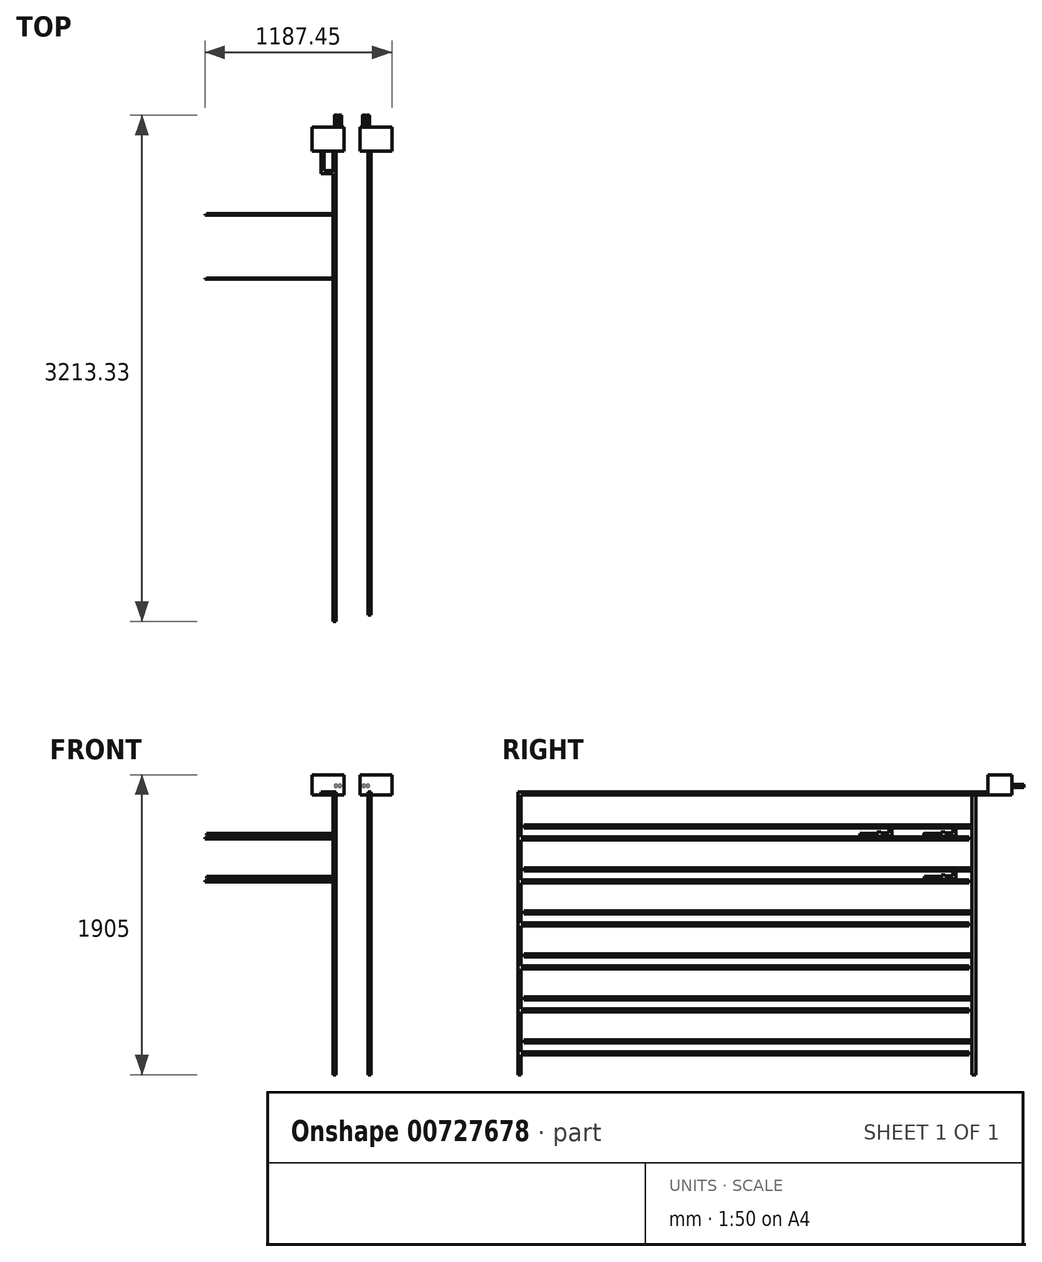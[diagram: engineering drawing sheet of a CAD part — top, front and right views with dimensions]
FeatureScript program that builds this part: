
annotation { "Feature Type Name" : "Feature", "Feature Type Description" : "" }
export const myFeature = defineFeature(function(context is Context, id is Id, definition is map)
    precondition{}
    {
        {
            var Q0;
            Q0=qCreatedBy(makeId("Top.planeOp"),FACE);
            var sketch = newSketch(context, id + "F0", { "sketchPlane" : qUnion([Q0])});
            skLineSegment(sketch, "E0.bottom", {"start": v(0, 0) * mm, "end": v(-1117.6, 0) * mm});
            skLineSegment(sketch, "E0.top", {"start": v(0, 2844.8) * mm, "end": v(-1117.6, 2844.8) * mm});
            skLineSegment(sketch, "E0.right", {"start": v(-1117.6, 0) * mm, "end": v(-1117.6, 2844.8) * mm});
            skLineSegment(sketch, "E1.bottom", {"start": v(0, 0) * mm, "end": v(1117.6, 0) * mm});
            skLineSegment(sketch, "E1.top", {"start": v(0, 2844.8) * mm, "end": v(1117.6, 2844.8) * mm});
            skLineSegment(sketch, "E1.right", {"start": v(1117.6, 0) * mm, "end": v(1117.6, 2844.8) * mm});
            skLineSegment(sketch, "E2.bottom", {"start": v(-101.6, 2844.8) * mm, "end": v(101.6, 2844.8) * mm});
            skLineSegment(sketch, "E2.top", {"start": v(-101.6, 0) * mm, "end": v(101.6, 0) * mm});
            skLineSegment(sketch, "E2.left", {"start": v(-101.6, 2641.6) * mm, "end": v(-101.6, 203.2) * mm});
            skLineSegment(sketch, "E2.right", {"start": v(101.6, 2641.6) * mm, "end": v(101.6, 203.2) * mm});
            skLineSegment(sketch, "E3", {"start": v(-1117.6, 2641.6) * mm, "end": v(-101.6, 2641.6) * mm});
            skLineSegment(sketch, "E4", {"start": v(-1117.6, 2235.2) * mm, "end": v(-101.6, 2235.2) * mm});
            skLineSegment(sketch, "E5", {"start": v(-1117.6, 1828.8) * mm, "end": v(-101.6, 1828.8) * mm});
            skLineSegment(sketch, "E6", {"start": v(-1117.6, 1422.4) * mm, "end": v(-101.6, 1422.4) * mm});
            skLineSegment(sketch, "E7", {"start": v(-1117.6, 1016) * mm, "end": v(-101.6, 1016) * mm});
            skLineSegment(sketch, "E8", {"start": v(-1117.6, 609.6) * mm, "end": v(-101.6, 609.6) * mm});
            skLineSegment(sketch, "E9", {"start": v(-1117.6, 203.2) * mm, "end": v(-101.6, 203.2) * mm});
            skLineSegment(sketch, "E10.trimOffspring", {"start": v(101.6, 2641.6) * mm, "end": v(1117.6, 2641.6) * mm});
            skLineSegment(sketch, "E11.trimOffspring", {"start": v(101.6, 2235.2) * mm, "end": v(1117.6, 2235.2) * mm});
            skLineSegment(sketch, "E12.trimOffspring", {"start": v(101.6, 1828.8) * mm, "end": v(1117.6, 1828.8) * mm});
            skLineSegment(sketch, "E13.trimOffspring", {"start": v(101.6, 1422.4) * mm, "end": v(1117.6, 1422.4) * mm});
            skLineSegment(sketch, "E14.trimOffspring", {"start": v(101.6, 1016) * mm, "end": v(1117.6, 1016) * mm});
            skLineSegment(sketch, "E15.trimOffspring", {"start": v(101.6, 609.6) * mm, "end": v(1117.6, 609.6) * mm});
            skLineSegment(sketch, "E16.trimOffspring", {"start": v(101.6, 203.2) * mm, "end": v(1117.6, 203.2) * mm});
            skLineSegment(sketch, "E17", {"start": v(-101.6, 2641.6) * mm, "end": v(101.6, 2641.6) * mm});
            skLineSegment(sketch, "E18.bottom", {"start": v(3130.62, 2641.6) * mm, "end": v(3333.82, 2641.6) * mm});
            skLineSegment(sketch, "E18.top", {"start": v(3130.62, 2794) * mm, "end": v(3333.82, 2794) * mm});
            skLineSegment(sketch, "E18.left", {"start": v(3130.62, 2641.6) * mm, "end": v(3130.62, 2794) * mm});
            skLineSegment(sketch, "E18.right", {"start": v(3333.82, 2641.6) * mm, "end": v(3333.82, 2794) * mm});
            skLineSegment(sketch, "E19.bottom", {"start": v(3435.42, 2641.6) * mm, "end": v(3638.62, 2641.6) * mm});
            skLineSegment(sketch, "E19.top", {"start": v(3435.42, 2794) * mm, "end": v(3638.62, 2794) * mm});
            skLineSegment(sketch, "E19.left", {"start": v(3435.42, 2641.6) * mm, "end": v(3435.42, 2794) * mm});
            skLineSegment(sketch, "E19.right", {"start": v(3638.62, 2641.6) * mm, "end": v(3638.62, 2794) * mm});
            skLineSegment(sketch, "E20", {"start": v(-812.8, 2641.6) * mm, "end": v(-812.8, 203.2) * mm});
            skLineSegment(sketch, "E21", {"start": v(-609.6, 2641.6) * mm, "end": v(-609.6, 203.2) * mm});
            skSolve(sketch);
        }
        {
            var Q0;
            Q0=makeQuery(id+"F0.imprint","IMPRINT",FACE,{"disambiguationData":[TD([[makeQuery(id+"F0.imprint","IMPRINT",EDGE,{"derivedFrom":sQuery(id+"F0.wireOp",EDGE,"E18.bottom")}),1.0]])]});
            extrude(context, id + "F1", {"entities" : qUnion([Q0]), "depth" : 127 * mm, "offsetDistance" : 25.4 * mm});
        }
        {
            var Q0;
            Q0=makeQuery(id+"F0.imprint","IMPRINT",FACE,{"disambiguationData":[TD([[makeQuery(id+"F0.imprint","IMPRINT",EDGE,{"derivedFrom":sQuery(id+"F0.wireOp",EDGE,"E19.bottom")}),1.0]])]});
            extrude(context, id + "F2", {"entities" : qUnion([Q0]), "depth" : 127 * mm, "offsetDistance" : 25.4 * mm});
        }
        {
            var Q0;
            Q0=makeQuery(id+"F1.opExtrude","SWEPT_FACE",FACE,{"disambiguationData":[OSD([sQuery(id+"F0.wireOp",EDGE,"E18.bottom")])]});
            var sketch = newSketch(context, id + "F3", { "sketchPlane" : qUnion([Q0])});
            skLineSegment(sketch, "E22.bottom", {"start": v(3283.02, 0) * mm, "end": v(3263.97, 0) * mm});
            skLineSegment(sketch, "E22.top", {"start": v(3283.02, 19.05) * mm, "end": v(3263.97, 19.05) * mm});
            skLineSegment(sketch, "E22.left", {"start": v(3283.02, 0) * mm, "end": v(3283.02, 19.05) * mm});
            skLineSegment(sketch, "E22.right", {"start": v(3263.97, 0) * mm, "end": v(3263.97, 19.05) * mm});
            skPoint(sketch, "E23.top.end.orphan", {"position": v(3416.06, 19.05) * mm});
            skPoint(sketch, "E23.left.start.orphan", {"position": v(3397.68, 0) * mm});
            skLineSegment(sketch, "E24.bottom", {"start": v(3486.22, 0) * mm, "end": v(3505.27, 0) * mm});
            skLineSegment(sketch, "E24.top", {"start": v(3486.22, 19.05) * mm, "end": v(3505.27, 19.05) * mm});
            skLineSegment(sketch, "E24.left", {"start": v(3486.22, 0) * mm, "end": v(3486.22, 19.05) * mm});
            skLineSegment(sketch, "E24.right", {"start": v(3505.27, 0) * mm, "end": v(3505.27, 19.05) * mm});
            skSolve(sketch);
        }
        {
            var Q0;
            Q0 = qSketchRegion(id + "F3", true);
            extrude(context, id + "F4", {"entities" : qUnion([Q0]), "depth" : 101.6 * mm, "offsetDistance" : 25.4 * mm});
        }
        {
            var Q0;
            Q0=makeQuery(id+"F4.opExtrude","SWEPT_FACE",FACE,{"disambiguationData":[OSD([sQuery(id+"F3.wireOp",EDGE,"E22.bottom")])]});
            var sketch = newSketch(context, id + "F5", { "sketchPlane" : qUnion([Q0])});
            skLineSegment(sketch, "E25.bottom", {"start": v(3263.97, -2540) * mm, "end": v(3283.02, -2540) * mm});
            skLineSegment(sketch, "E25.top", {"start": v(3263.97, -2565.4) * mm, "end": v(3283.02, -2565.4) * mm});
            skLineSegment(sketch, "E25.left", {"start": v(3263.97, -2540) * mm, "end": v(3263.97, -2565.4) * mm});
            skLineSegment(sketch, "E25.right", {"start": v(3283.02, -2540) * mm, "end": v(3283.02, -2565.4) * mm});
            skLineSegment(sketch, "E26.bottom", {"start": v(3486.22, -2540) * mm, "end": v(3505.27, -2540) * mm});
            skLineSegment(sketch, "E26.top", {"start": v(3486.22, -2565.4) * mm, "end": v(3505.27, -2565.4) * mm});
            skLineSegment(sketch, "E26.left", {"start": v(3486.22, -2540) * mm, "end": v(3486.22, -2565.4) * mm});
            skLineSegment(sketch, "E26.right", {"start": v(3505.27, -2540) * mm, "end": v(3505.27, -2565.4) * mm});
            skSolve(sketch);
        }
        {
            var Q0;
            Q0 = qSketchRegion(id + "F5", true);
            extrude(context, id + "F6", {"entities" : qUnion([Q0]), "depth" : 1778 * mm, "offsetDistance" : 25.4 * mm});
        }
        {
            var Q0;
            Q0=makeQuery(id+"F6.opExtrude","SWEPT_FACE",FACE,{"disambiguationData":[OSD([sQuery(id+"F5.wireOp",EDGE,"E25.bottom")])]});
            var sketch = newSketch(context, id + "F7", { "sketchPlane" : qUnion([Q0])});
            skLineSegment(sketch, "E27.bottom", {"start": v(3263.97, -190.5) * mm, "end": v(3283.02, -190.5) * mm});
            skLineSegment(sketch, "E27.top", {"start": v(3263.97, -209.55) * mm, "end": v(3283.02, -209.55) * mm});
            skLineSegment(sketch, "E27.left", {"start": v(3263.97, -190.5) * mm, "end": v(3263.97, -209.55) * mm});
            skLineSegment(sketch, "E27.right", {"start": v(3283.02, -190.5) * mm, "end": v(3283.02, -209.55) * mm});
            skLineSegment(sketch, "E28.bottom", {"start": v(3263.97, -463.55) * mm, "end": v(3283.02, -463.55) * mm});
            skLineSegment(sketch, "E28.top", {"start": v(3263.97, -482.6) * mm, "end": v(3283.02, -482.6) * mm});
            skLineSegment(sketch, "E28.left", {"start": v(3263.97, -463.55) * mm, "end": v(3263.97, -482.6) * mm});
            skLineSegment(sketch, "E28.right", {"start": v(3283.02, -463.55) * mm, "end": v(3283.02, -482.6) * mm});
            skLineSegment(sketch, "E29.bottom", {"start": v(3263.97, -736.6) * mm, "end": v(3283.02, -736.6) * mm});
            skLineSegment(sketch, "E29.top", {"start": v(3263.97, -755.65) * mm, "end": v(3283.02, -755.65) * mm});
            skLineSegment(sketch, "E29.left", {"start": v(3263.97, -736.6) * mm, "end": v(3263.97, -755.65) * mm});
            skLineSegment(sketch, "E29.right", {"start": v(3283.02, -736.6) * mm, "end": v(3283.02, -755.65) * mm});
            skLineSegment(sketch, "E30.bottom", {"start": v(3263.97, -1009.65) * mm, "end": v(3283.02, -1009.65) * mm});
            skLineSegment(sketch, "E30.top", {"start": v(3263.97, -1028.7) * mm, "end": v(3283.02, -1028.7) * mm});
            skLineSegment(sketch, "E30.left", {"start": v(3263.97, -1009.65) * mm, "end": v(3263.97, -1028.7) * mm});
            skLineSegment(sketch, "E30.right", {"start": v(3283.02, -1009.65) * mm, "end": v(3283.02, -1028.7) * mm});
            skLineSegment(sketch, "E31.bottom", {"start": v(3263.97, -1282.7) * mm, "end": v(3283.02, -1282.7) * mm});
            skLineSegment(sketch, "E31.top", {"start": v(3263.97, -1301.75) * mm, "end": v(3283.02, -1301.75) * mm});
            skLineSegment(sketch, "E31.left", {"start": v(3263.97, -1282.7) * mm, "end": v(3263.97, -1301.75) * mm});
            skLineSegment(sketch, "E31.right", {"start": v(3283.02, -1282.7) * mm, "end": v(3283.02, -1301.75) * mm});
            skLineSegment(sketch, "E32.bottom", {"start": v(3263.97, -1555.75) * mm, "end": v(3283.02, -1555.75) * mm});
            skLineSegment(sketch, "E32.top", {"start": v(3263.97, -1574.8) * mm, "end": v(3283.02, -1574.8) * mm});
            skLineSegment(sketch, "E32.left", {"start": v(3263.97, -1555.75) * mm, "end": v(3263.97, -1574.8) * mm});
            skLineSegment(sketch, "E32.right", {"start": v(3283.02, -1555.75) * mm, "end": v(3283.02, -1574.8) * mm});
            skLineSegment(sketch, "E33.bottom", {"start": v(3486.22, -190.5) * mm, "end": v(3505.27, -190.5) * mm});
            skLineSegment(sketch, "E33.top", {"start": v(3486.22, -209.55) * mm, "end": v(3505.27, -209.55) * mm});
            skLineSegment(sketch, "E33.left", {"start": v(3486.22, -190.5) * mm, "end": v(3486.22, -209.55) * mm});
            skLineSegment(sketch, "E33.right", {"start": v(3505.27, -190.5) * mm, "end": v(3505.27, -209.55) * mm});
            skLineSegment(sketch, "E34.bottom", {"start": v(3486.22, -463.55) * mm, "end": v(3505.27, -463.55) * mm});
            skLineSegment(sketch, "E34.top", {"start": v(3486.22, -482.6) * mm, "end": v(3505.27, -482.6) * mm});
            skLineSegment(sketch, "E34.left", {"start": v(3486.22, -463.55) * mm, "end": v(3486.22, -482.6) * mm});
            skLineSegment(sketch, "E34.right", {"start": v(3505.27, -463.55) * mm, "end": v(3505.27, -482.6) * mm});
            skLineSegment(sketch, "E35.bottom", {"start": v(3486.22, -736.6) * mm, "end": v(3505.27, -736.6) * mm});
            skLineSegment(sketch, "E35.top", {"start": v(3486.22, -755.65) * mm, "end": v(3505.27, -755.65) * mm});
            skLineSegment(sketch, "E35.left", {"start": v(3486.22, -736.6) * mm, "end": v(3486.22, -755.65) * mm});
            skLineSegment(sketch, "E35.right", {"start": v(3505.27, -736.6) * mm, "end": v(3505.27, -755.65) * mm});
            skLineSegment(sketch, "E36.bottom", {"start": v(3486.22, -1009.65) * mm, "end": v(3505.27, -1009.65) * mm});
            skLineSegment(sketch, "E36.top", {"start": v(3486.22, -1028.7) * mm, "end": v(3505.27, -1028.7) * mm});
            skLineSegment(sketch, "E36.left", {"start": v(3486.22, -1009.65) * mm, "end": v(3486.22, -1028.7) * mm});
            skLineSegment(sketch, "E36.right", {"start": v(3505.27, -1009.65) * mm, "end": v(3505.27, -1028.7) * mm});
            skLineSegment(sketch, "E37.bottom", {"start": v(3486.22, -1282.7) * mm, "end": v(3505.27, -1282.7) * mm});
            skLineSegment(sketch, "E37.top", {"start": v(3486.22, -1301.75) * mm, "end": v(3505.27, -1301.75) * mm});
            skLineSegment(sketch, "E37.left", {"start": v(3486.22, -1282.7) * mm, "end": v(3486.22, -1301.75) * mm});
            skLineSegment(sketch, "E37.right", {"start": v(3505.27, -1282.7) * mm, "end": v(3505.27, -1301.75) * mm});
            skLineSegment(sketch, "E38.bottom", {"start": v(3486.22, -1555.75) * mm, "end": v(3505.27, -1555.75) * mm});
            skLineSegment(sketch, "E38.top", {"start": v(3486.22, -1574.8) * mm, "end": v(3505.27, -1574.8) * mm});
            skLineSegment(sketch, "E38.left", {"start": v(3486.22, -1555.75) * mm, "end": v(3486.22, -1574.8) * mm});
            skLineSegment(sketch, "E38.right", {"start": v(3505.27, -1555.75) * mm, "end": v(3505.27, -1574.8) * mm});
            skSolve(sketch);
        }
        {
            var Q0;
            Q0 = qSketchRegion(id + "F7", true);
            extrude(context, id + "F8", {"entities" : qUnion([Q0]), "depth" : 2844.8 * mm, "offsetDistance" : 25.4 * mm});
        }
        {
            var Q0;
            Q0=makeQuery(id+"F8.opExtrude","SWEPT_FACE",FACE,{"disambiguationData":[OSD([sQuery(id+"F7.wireOp",EDGE,"E27.top")])]});
            var sketch = newSketch(context, id + "F9", { "sketchPlane" : qUnion([Q0])});
            skLineSegment(sketch, "E39.bottom", {"start": v(3263.97, -2438.4) * mm, "end": v(3283.02, -2438.4) * mm});
            skLineSegment(sketch, "E39.top", {"start": v(3263.97, -2419.35) * mm, "end": v(3283.02, -2419.35) * mm});
            skLineSegment(sketch, "E39.left", {"start": v(3263.97, -2438.4) * mm, "end": v(3263.97, -2419.35) * mm});
            skLineSegment(sketch, "E39.right", {"start": v(3283.02, -2438.4) * mm, "end": v(3283.02, -2419.35) * mm});
            skSolve(sketch);
        }
        {
            var Q0;
            Q0 = qSketchRegion(id + "F9", true);
            extrude(context, id + "F10", {"entities" : qUnion([Q0]), "operationType" : NewBodyOperationType.ADD, "depth" : 50.8 * mm, "offsetDistance" : 25.4 * mm});
        }
        {
            var Q0;
            Q0=makeQuery(id+"F10.opExtrude","SWEPT_FACE",FACE,{"disambiguationData":[OSD([sQuery(id+"F9.wireOp",EDGE,"E39.top")])]});
            var sketch = newSketch(context, id + "F11", { "sketchPlane" : qUnion([Q0])});
            skLineSegment(sketch, "E40.bottom", {"start": v(3263.97, -260.35) * mm, "end": v(3283.02, -260.35) * mm});
            skLineSegment(sketch, "E40.top", {"start": v(3263.97, -241.3) * mm, "end": v(3283.02, -241.3) * mm});
            skLineSegment(sketch, "E40.left", {"start": v(3263.97, -260.35) * mm, "end": v(3263.97, -241.3) * mm});
            skLineSegment(sketch, "E40.right", {"start": v(3283.02, -260.35) * mm, "end": v(3283.02, -241.3) * mm});
            skSolve(sketch);
        }
        {
            var Q0;
            Q0 = qSketchRegion(id + "F11", true);
            extrude(context, id + "F12", {"entities" : qUnion([Q0]), "operationType" : NewBodyOperationType.ADD, "depth" : 50.8 * mm, "offsetDistance" : 25.4 * mm});
        }
        {
            var Q0;
            Q0=makeQuery(id+"F12.opExtrude","CAP_FACE",FACE,{"disambiguationData":[OSD([sQuery(id+"F11.wireOp",EDGE,"E40.bottom"),sQuery(id+"F11.wireOp",EDGE,"E40.top"),sQuery(id+"F11.wireOp",EDGE,"E40.left"),sQuery(id+"F11.wireOp",EDGE,"E40.right")])],"isStart":false});
            var sketch = newSketch(context, id + "F13", { "sketchPlane" : qUnion([Q0])});
            skLineSegment(sketch, "E41.bottom", {"start": v(3263.97, -264.58) * mm, "end": v(3283.02, -264.58) * mm});
            skLineSegment(sketch, "E41.top", {"start": v(3263.97, -237.07) * mm, "end": v(3283.02, -237.07) * mm});
            skLineSegment(sketch, "E41.left", {"start": v(3263.97, -264.58) * mm, "end": v(3263.97, -237.07) * mm});
            skLineSegment(sketch, "E41.right", {"start": v(3283.02, -264.58) * mm, "end": v(3283.02, -237.07) * mm});
            skSolve(sketch);
        }
        {
            var Q0;
            Q0 = qSketchRegion(id + "F13", true);
            extrude(context, id + "F14", {"entities" : qUnion([Q0]), "operationType" : NewBodyOperationType.ADD, "depth" : 25.4 * mm, "offsetDistance" : 25.4 * mm});
        }
        {
            var Q0;
            Q0=makeQuery(id+"F14.opExtrude","CAP_FACE",FACE,{"disambiguationData":[OSD([sQuery(id+"F13.wireOp",EDGE,"E41.bottom"),sQuery(id+"F13.wireOp",EDGE,"E41.top"),sQuery(id+"F13.wireOp",EDGE,"E41.left"),sQuery(id+"F13.wireOp",EDGE,"E41.right")])],"isStart":false});
            var sketch = newSketch(context, id + "F15", { "sketchPlane" : qUnion([Q0])});
            skCircle(sketch, "E42", {"center": v(3273.5, -250.83) * mm, "radius": 4.23 * mm});
            skSolve(sketch);
        }
        {
            var Q0;
            Q0 = qSketchRegion(id + "F15", true);
            extrude(context, id + "F16", {"entities" : qUnion([Q0]), "operationType" : NewBodyOperationType.ADD, "depth" : 107.95 * mm, "offsetDistance" : 25.4 * mm});
        }
        {
            var Q0;
            Q0=makeQuery(id+"F14.boolean.opBoolean","MERGE",FACE,{"derivedFrom":[makeQuery(id+"F12.boolean.opBoolean","MERGE",FACE,{"derivedFrom":[makeQuery(id+"F10.boolean.opBoolean","MERGE",FACE,{"derivedFrom":[makeQuery(id+"F8.opExtrude","SWEPT_FACE",FACE,{"disambiguationData":[OSD([sQuery(id+"F7.wireOp",EDGE,"E27.left")])]}),makeQuery(id+"F10.opExtrude","SWEPT_FACE",FACE,{"disambiguationData":[OSD([sQuery(id+"F9.wireOp",EDGE,"E39.left")])]})]}),makeQuery(id+"F12.opExtrude","SWEPT_FACE",FACE,{"disambiguationData":[OSD([sQuery(id+"F11.wireOp",EDGE,"E40.left")])]})]}),makeQuery(id+"F14.opExtrude","SWEPT_FACE",FACE,{"disambiguationData":[OSD([sQuery(id+"F13.wireOp",EDGE,"E41.left")])]})]});
            cPlane(context, id + "F17", {"entities" : qUnion([Q0]), "cplaneType" : CPlaneType.OFFSET, "offset" : 9.52 * mm, "oppositeDirection" : true, "width" : 152.4 * mm, "height" : 152.4 * mm});
        }
        {
            var Q0;
            Q0=qCreatedBy(id+"F17.planeOp",FACE);
            var sketch = newSketch(context, id + "F18", { "sketchPlane" : qUnion([Q0])});
            skCircle(sketch, "E43", {"center": v(-2239.43, -250.77) * mm, "radius": 4.23 * mm});
            skSolve(sketch);
        }
        {
            var Q0;
            Q0 = qSketchRegion(id + "F18", true);
            extrude(context, id + "F19", {"entities" : qUnion([Q0]), "operationType" : NewBodyOperationType.ADD, "depth" : 812.8 * mm, "offsetDistance" : 25.4 * mm});
        }
        {
            var Q0;
            {var subQ2=sQuery(id+"F7.wireOp",EDGE,"E27.top");Q0=makeQuery(id+"F10.boolean.opBoolean","SPLIT",FACE,{"disambiguationData":[TD([makeQuery(id+"F10.opExtrude","SWEPT_FACE",FACE,{"disambiguationData":[OSD([sQuery(id+"F9.wireOp",EDGE,"E39.top")])]})])],"derivedFrom":makeQuery(id+"F8.opExtrude","SWEPT_FACE",FACE,{"disambiguationData":[OSD([subQ2])]})});}
            var sketch = newSketch(context, id + "F20", { "sketchPlane" : qUnion([Q0])});
            skLineSegment(sketch, "E44.bottom", {"start": v(3263.97, -2032) * mm, "end": v(3283.02, -2032) * mm});
            skLineSegment(sketch, "E44.top", {"start": v(3263.97, -2012.95) * mm, "end": v(3283.02, -2012.95) * mm});
            skLineSegment(sketch, "E44.left", {"start": v(3263.97, -2032) * mm, "end": v(3263.97, -2012.95) * mm});
            skLineSegment(sketch, "E44.right", {"start": v(3283.02, -2032) * mm, "end": v(3283.02, -2012.95) * mm});
            skSolve(sketch);
        }
        {
            var Q0;
            Q0 = qSketchRegion(id + "F20", true);
            extrude(context, id + "F21", {"entities" : qUnion([Q0]), "operationType" : NewBodyOperationType.ADD, "depth" : 50.8 * mm, "offsetDistance" : 25.4 * mm});
        }
        {
            var Q0;
            Q0=makeQuery(id+"F21.opExtrude","SWEPT_FACE",FACE,{"disambiguationData":[OSD([sQuery(id+"F20.wireOp",EDGE,"E44.top")])]});
            var sketch = newSketch(context, id + "F22", { "sketchPlane" : qUnion([Q0])});
            skLineSegment(sketch, "E45.bottom", {"start": v(3263.97, -260.35) * mm, "end": v(3283.02, -260.35) * mm});
            skLineSegment(sketch, "E45.top", {"start": v(3263.97, -241.3) * mm, "end": v(3283.02, -241.3) * mm});
            skLineSegment(sketch, "E45.left", {"start": v(3263.97, -260.35) * mm, "end": v(3263.97, -241.3) * mm});
            skLineSegment(sketch, "E45.right", {"start": v(3283.02, -260.35) * mm, "end": v(3283.02, -241.3) * mm});
            skSolve(sketch);
        }
        {
            var Q0;
            Q0 = qSketchRegion(id + "F22", true);
            extrude(context, id + "F23", {"entities" : qUnion([Q0]), "operationType" : NewBodyOperationType.ADD, "depth" : 50.8 * mm, "offsetDistance" : 25.4 * mm});
        }
        {
            var Q0;
            Q0=makeQuery(id+"F23.opExtrude","CAP_FACE",FACE,{"disambiguationData":[OSD([sQuery(id+"F22.wireOp",EDGE,"E45.bottom"),sQuery(id+"F22.wireOp",EDGE,"E45.top"),sQuery(id+"F22.wireOp",EDGE,"E45.left"),sQuery(id+"F22.wireOp",EDGE,"E45.right")])],"isStart":false});
            var sketch = newSketch(context, id + "F24", { "sketchPlane" : qUnion([Q0])});
            skLineSegment(sketch, "E46.bottom", {"start": v(3263.97, -237.07) * mm, "end": v(3283.02, -237.07) * mm});
            skLineSegment(sketch, "E46.top", {"start": v(3263.97, -264.58) * mm, "end": v(3283.02, -264.58) * mm});
            skLineSegment(sketch, "E46.left", {"start": v(3263.97, -237.07) * mm, "end": v(3263.97, -264.58) * mm});
            skLineSegment(sketch, "E46.right", {"start": v(3283.02, -237.07) * mm, "end": v(3283.02, -264.58) * mm});
            skSolve(sketch);
        }
        {
            var Q0;
            Q0 = qSketchRegion(id + "F24", true);
            extrude(context, id + "F25", {"entities" : qUnion([Q0]), "operationType" : NewBodyOperationType.ADD, "depth" : 25.4 * mm, "offsetDistance" : 25.4 * mm});
        }
        {
            var Q0;
            Q0=makeQuery(id+"F25.opExtrude","CAP_FACE",FACE,{"disambiguationData":[OSD([sQuery(id+"F24.wireOp",EDGE,"E46.bottom"),sQuery(id+"F24.wireOp",EDGE,"E46.top"),sQuery(id+"F24.wireOp",EDGE,"E46.left"),sQuery(id+"F24.wireOp",EDGE,"E46.right")])],"isStart":false});
            var sketch = newSketch(context, id + "F26", { "sketchPlane" : qUnion([Q0])});
            skCircle(sketch, "E47", {"center": v(3273.5, -250.83) * mm, "radius": 4.23 * mm});
            skSolve(sketch);
        }
        {
            var Q0;
            Q0 = qSketchRegion(id + "F26", true);
            extrude(context, id + "F27", {"entities" : qUnion([Q0]), "operationType" : NewBodyOperationType.ADD, "depth" : 107.95 * mm, "offsetDistance" : 25.4 * mm});
        }
        {
            var Q0;
            Q0=qCreatedBy(id+"F17.planeOp",FACE);
            var sketch = newSketch(context, id + "F28", { "sketchPlane" : qUnion([Q0])});
            skCircle(sketch, "E48", {"center": v(-1833.03, -250.83) * mm, "radius": 4.23 * mm});
            skSolve(sketch);
        }
        {
            var Q0;
            Q0 = qSketchRegion(id + "F28", true);
            extrude(context, id + "F29", {"entities" : qUnion([Q0]), "operationType" : NewBodyOperationType.ADD, "depth" : 812.8 * mm, "offsetDistance" : 25.4 * mm});
        }
        {
            var Q0;
            Q0=makeQuery(id+"F25.boolean.opBoolean","MERGE",FACE,{"derivedFrom":[makeQuery(id+"F23.boolean.opBoolean","MERGE",FACE,{"derivedFrom":[makeQuery(id+"F21.boolean.opBoolean","MERGE",FACE,{"derivedFrom":[makeQuery(id+"F14.boolean.opBoolean","MERGE",FACE,{"derivedFrom":[makeQuery(id+"F12.boolean.opBoolean","MERGE",FACE,{"derivedFrom":[makeQuery(id+"F10.boolean.opBoolean","MERGE",FACE,{"derivedFrom":[makeQuery(id+"F8.opExtrude","SWEPT_FACE",FACE,{"disambiguationData":[OSD([sQuery(id+"F7.wireOp",EDGE,"E27.left")])]}),makeQuery(id+"F10.opExtrude","SWEPT_FACE",FACE,{"disambiguationData":[OSD([sQuery(id+"F9.wireOp",EDGE,"E39.left")])]})]}),makeQuery(id+"F12.opExtrude","SWEPT_FACE",FACE,{"disambiguationData":[OSD([sQuery(id+"F11.wireOp",EDGE,"E40.left")])]})]}),makeQuery(id+"F14.opExtrude","SWEPT_FACE",FACE,{"disambiguationData":[OSD([sQuery(id+"F13.wireOp",EDGE,"E41.left")])]})]}),makeQuery(id+"F21.opExtrude","SWEPT_FACE",FACE,{"disambiguationData":[OSD([sQuery(id+"F20.wireOp",EDGE,"E44.left")])]})]}),makeQuery(id+"F23.opExtrude","SWEPT_FACE",FACE,{"disambiguationData":[OSD([sQuery(id+"F22.wireOp",EDGE,"E45.left")])]})]}),makeQuery(id+"F25.opExtrude","SWEPT_FACE",FACE,{"disambiguationData":[OSD([sQuery(id+"F24.wireOp",EDGE,"E46.left")])]})]});
            var sketch = newSketch(context, id + "F30", { "sketchPlane" : qUnion([Q0])});
            skLineSegment(sketch, "E49.bottom", {"start": v(-2438.4, -483.36) * mm, "end": v(-2419.35, -483.36) * mm});
            skLineSegment(sketch, "E49.top", {"start": v(-2438.4, -533.4) * mm, "end": v(-2419.35, -533.4) * mm});
            skLineSegment(sketch, "E49.left", {"start": v(-2438.4, -483.36) * mm, "end": v(-2438.4, -533.4) * mm});
            skLineSegment(sketch, "E49.right", {"start": v(-2419.35, -483.36) * mm, "end": v(-2419.35, -514.35) * mm});
            skLineSegment(sketch, "E50.bottom", {"start": v(-2419.35, -533.4) * mm, "end": v(-2368.55, -533.4) * mm});
            skLineSegment(sketch, "E50.top", {"start": v(-2419.35, -514.35) * mm, "end": v(-2368.55, -514.35) * mm});
            skLineSegment(sketch, "E51.bottom", {"start": v(-2368.55, -510.12) * mm, "end": v(-2346.2, -510.12) * mm});
            skLineSegment(sketch, "E51.top", {"start": v(-2368.55, -537.62) * mm, "end": v(-2346.2, -537.62) * mm});
            skLineSegment(sketch, "E51.left", {"start": v(-2368.55, -510.12) * mm, "end": v(-2368.55, -514.35) * mm});
            skLineSegment(sketch, "E51.right", {"start": v(-2346.2, -510.12) * mm, "end": v(-2346.2, -537.62) * mm});
            skLineSegment(sketch, "E52.trimOffspring", {"start": v(-2368.55, -533.4) * mm, "end": v(-2368.55, -537.62) * mm});
            skSolve(sketch);
        }
        {
            var Q0;
            Q0 = qSketchRegion(id + "F30", true);
            extrude(context, id + "F31", {"entities" : qUnion([Q0]), "oppositeDirection" : true, "depth" : 19.05 * mm, "offsetDistance" : 25.4 * mm});
        }
        {
            var Q0;
            Q0=makeQuery(id+"F31.opExtrude","SWEPT_FACE",FACE,{"disambiguationData":[OSD([sQuery(id+"F30.wireOp",EDGE,"E51.right")])]});
            var sketch = newSketch(context, id + "F32", { "sketchPlane" : qUnion([Q0])});
            skCircle(sketch, "E53", {"center": v(3273.5, -523.87) * mm, "radius": 4.23 * mm});
            skPoint(sketch, "E53.centerSnap0", {"position": v(3273.5, -537.62) * mm});
            skPoint(sketch, "E53.centerSnap1", {"position": v(3263.97, -523.87) * mm});
            skSolve(sketch);
        }
        {
            var Q0;
            Q0 = qSketchRegion(id + "F32", true);
            extrude(context, id + "F33", {"entities" : qUnion([Q0]), "operationType" : NewBodyOperationType.ADD, "depth" : 107.95 * mm, "offsetDistance" : 25.4 * mm});
        }
        {
            var Q0;
            Q0=qCreatedBy(id+"F17.planeOp",FACE);
            var sketch = newSketch(context, id + "F34", { "sketchPlane" : qUnion([Q0])});
            skCircle(sketch, "E54", {"center": v(-2242.49, -523.87) * mm, "radius": 4.23 * mm});
            skSolve(sketch);
        }
        {
            var Q0;
            Q0 = qSketchRegion(id + "F34", true);
            extrude(context, id + "F35", {"entities" : qUnion([Q0]), "operationType" : NewBodyOperationType.ADD, "depth" : 812.8 * mm, "offsetDistance" : 25.4 * mm});
        }
        {
            var Q0;
            Q0=makeQuery(id+"F6.opExtrude","CAP_FACE",FACE,{"disambiguationData":[OSD([sQuery(id+"F5.wireOp",EDGE,"E25.bottom"),sQuery(id+"F5.wireOp",EDGE,"E25.top"),sQuery(id+"F5.wireOp",EDGE,"E25.left"),sQuery(id+"F5.wireOp",EDGE,"E25.right")])],"isStart":false});
            var sketch = newSketch(context, id + "F36", { "sketchPlane" : qUnion([Q0])});
            skPoint(sketch, "E55.firstSnap0", {"position": v(3263.97, -2552.7) * mm});
            skLineSegment(sketch, "E55.bottom", {"start": v(3263.97, 324.08) * mm, "end": v(3283.02, 324.08) * mm});
            skLineSegment(sketch, "E55.top", {"start": v(3263.97, 343.13) * mm, "end": v(3283.02, 343.13) * mm});
            skLineSegment(sketch, "E55.left", {"start": v(3263.97, 324.08) * mm, "end": v(3263.97, 343.13) * mm});
            skLineSegment(sketch, "E55.right", {"start": v(3283.02, 324.08) * mm, "end": v(3283.02, 343.13) * mm});
            skSolve(sketch);
        }
        {
            var Q0;
            Q0 = qSketchRegion(id + "F36", true);
            extrude(context, id + "F37", {"entities" : qUnion([Q0]), "oppositeDirection" : true, "depth" : 1778 * mm, "offsetDistance" : 25.4 * mm});
        }
        {
            var Q0;
            Q0=makeQuery(id+"F37.opExtrude","SWEPT_FACE",FACE,{"disambiguationData":[OSD([sQuery(id+"F36.wireOp",EDGE,"E55.bottom")])]});
            var sketch = newSketch(context, id + "F38", { "sketchPlane" : qUnion([Q0])});
            skLineSegment(sketch, "E56.bottom", {"start": v(-3263.97, -1651) * mm, "end": v(-3283.02, -1651) * mm});
            skLineSegment(sketch, "E56.top", {"start": v(-3263.97, -1631.95) * mm, "end": v(-3283.02, -1631.95) * mm});
            skLineSegment(sketch, "E56.left", {"start": v(-3263.97, -1651) * mm, "end": v(-3263.97, -1631.95) * mm});
            skLineSegment(sketch, "E56.right", {"start": v(-3283.02, -1651) * mm, "end": v(-3283.02, -1631.95) * mm});
            skLineSegment(sketch, "E57.bottom", {"start": v(-3283.02, -1358.9) * mm, "end": v(-3263.97, -1358.9) * mm});
            skLineSegment(sketch, "E57.top", {"start": v(-3283.02, -1377.95) * mm, "end": v(-3263.97, -1377.95) * mm});
            skLineSegment(sketch, "E57.left", {"start": v(-3283.02, -1358.9) * mm, "end": v(-3283.02, -1377.95) * mm});
            skLineSegment(sketch, "E57.right", {"start": v(-3263.97, -1358.9) * mm, "end": v(-3263.97, -1377.95) * mm});
            skLineSegment(sketch, "E58.bottom", {"start": v(-3283.02, -1085.85) * mm, "end": v(-3263.97, -1085.85) * mm});
            skLineSegment(sketch, "E58.top", {"start": v(-3283.02, -1104.9) * mm, "end": v(-3263.97, -1104.9) * mm});
            skLineSegment(sketch, "E58.left", {"start": v(-3283.02, -1085.85) * mm, "end": v(-3283.02, -1104.9) * mm});
            skLineSegment(sketch, "E58.right", {"start": v(-3263.97, -1085.85) * mm, "end": v(-3263.97, -1104.9) * mm});
            skLineSegment(sketch, "E59.bottom", {"start": v(-3283.02, -812.8) * mm, "end": v(-3263.97, -812.8) * mm});
            skLineSegment(sketch, "E59.top", {"start": v(-3283.02, -831.85) * mm, "end": v(-3263.97, -831.85) * mm});
            skLineSegment(sketch, "E59.left", {"start": v(-3283.02, -812.8) * mm, "end": v(-3283.02, -831.85) * mm});
            skLineSegment(sketch, "E59.right", {"start": v(-3263.97, -812.8) * mm, "end": v(-3263.97, -831.85) * mm});
            skLineSegment(sketch, "E60.bottom", {"start": v(-3283.02, -539.75) * mm, "end": v(-3263.97, -539.75) * mm});
            skLineSegment(sketch, "E60.top", {"start": v(-3283.02, -558.8) * mm, "end": v(-3263.97, -558.8) * mm});
            skLineSegment(sketch, "E60.left", {"start": v(-3283.02, -539.75) * mm, "end": v(-3283.02, -558.8) * mm});
            skLineSegment(sketch, "E60.right", {"start": v(-3263.97, -539.75) * mm, "end": v(-3263.97, -558.8) * mm});
            skLineSegment(sketch, "E61.bottom", {"start": v(-3283.02, -266.7) * mm, "end": v(-3263.97, -266.7) * mm});
            skLineSegment(sketch, "E61.top", {"start": v(-3283.02, -285.75) * mm, "end": v(-3263.97, -285.75) * mm});
            skLineSegment(sketch, "E61.left", {"start": v(-3283.02, -266.7) * mm, "end": v(-3283.02, -285.75) * mm});
            skLineSegment(sketch, "E61.right", {"start": v(-3263.97, -266.7) * mm, "end": v(-3263.97, -285.75) * mm});
            skSolve(sketch);
        }
        {
            var Q0;
            Q0 = qSketchRegion(id + "F38", true);
            extrude(context, id + "F39", {"entities" : qUnion([Q0]), "operationType" : NewBodyOperationType.ADD, "depth" : 2844.8 * mm, "offsetDistance" : 25.4 * mm});
        }
        {
            var Q0;
            Q0=makeQuery(id+"F37.opExtrude","CAP_FACE",FACE,{"disambiguationData":[OSD([sQuery(id+"F36.wireOp",EDGE,"E55.bottom"),sQuery(id+"F36.wireOp",EDGE,"E55.top"),sQuery(id+"F36.wireOp",EDGE,"E55.left"),sQuery(id+"F36.wireOp",EDGE,"E55.right")])],"isStart":false});
            var sketch = newSketch(context, id + "F40", { "sketchPlane" : qUnion([Q0])});
            skLineSegment(sketch, "E62.bottom", {"start": v(3263.97, -343.13) * mm, "end": v(3283.02, -343.13) * mm});
            skLineSegment(sketch, "E62.top", {"start": v(3263.97, -324.08) * mm, "end": v(3283.02, -324.08) * mm});
            skLineSegment(sketch, "E62.left", {"start": v(3263.97, -343.13) * mm, "end": v(3263.97, -324.08) * mm});
            skLineSegment(sketch, "E62.right", {"start": v(3283.02, -343.13) * mm, "end": v(3283.02, -324.08) * mm});
            skSolve(sketch);
        }
        {
            var Q0;
            Q0 = qSketchRegion(id + "F40", true);
            extrude(context, id + "F41", {"entities" : qUnion([Q0]), "operationType" : NewBodyOperationType.ADD, "depth" : 19.05 * mm, "offsetDistance" : 25.4 * mm});
        }
        {
            var Q0;
            {var subQ2=sQuery(id+"F36.wireOp",EDGE,"E55.bottom");Q0=makeQuery(id+"F41.boolean.opBoolean","MERGE",FACE,{"derivedFrom":[makeQuery(id+"F39.boolean.opBoolean","SPLIT",FACE,{"disambiguationData":[TD([makeQuery(id+"F39.opExtrude","SWEPT_FACE",FACE,{"disambiguationData":[OSD([sQuery(id+"F38.wireOp",EDGE,"E61.bottom")])]})])],"derivedFrom":makeQuery(id+"F37.opExtrude","SWEPT_FACE",FACE,{"disambiguationData":[OSD([subQ2])]})}),makeQuery(id+"F41.opExtrude","SWEPT_FACE",FACE,{"disambiguationData":[OSD([sQuery(id+"F40.wireOp",EDGE,"E62.top")])]})]});}
            var sketch = newSketch(context, id + "F42", { "sketchPlane" : qUnion([Q0])});
            skLineSegment(sketch, "E63.bottom", {"start": v(-3283.02, 19.05) * mm, "end": v(-3263.97, 19.05) * mm});
            skLineSegment(sketch, "E63.top", {"start": v(-3283.02, 0) * mm, "end": v(-3263.97, 0) * mm});
            skLineSegment(sketch, "E63.left", {"start": v(-3283.02, 19.05) * mm, "end": v(-3283.02, 0) * mm});
            skLineSegment(sketch, "E63.right", {"start": v(-3263.97, 19.05) * mm, "end": v(-3263.97, 0) * mm});
            skSolve(sketch);
        }
        {
            var Q0;
            Q0 = qSketchRegion(id + "F42", true);
            extrude(context, id + "F43", {"entities" : qUnion([Q0]), "operationType" : NewBodyOperationType.ADD, "depth" : 2844.8 * mm, "offsetDistance" : 25.4 * mm});
        }
        {
            var Q0;
            Q0=makeQuery(id+"F43.boolean.opBoolean","MERGE",FACE,{"derivedFrom":[makeQuery(id+"F41.boolean.opBoolean","MERGE",FACE,{"derivedFrom":[makeQuery(id+"F39.boolean.opBoolean","MERGE",FACE,{"derivedFrom":[makeQuery(id+"F37.opExtrude","SWEPT_FACE",FACE,{"disambiguationData":[OSD([sQuery(id+"F36.wireOp",EDGE,"E55.left")])]}),makeQuery(id+"F39.opExtrude","SWEPT_FACE",FACE,{"disambiguationData":[OSD([sQuery(id+"F38.wireOp",EDGE,"E56.left")])]}),makeQuery(id+"F39.opExtrude","SWEPT_FACE",FACE,{"disambiguationData":[OSD([sQuery(id+"F38.wireOp",EDGE,"E57.right")])]}),makeQuery(id+"F39.opExtrude","SWEPT_FACE",FACE,{"disambiguationData":[OSD([sQuery(id+"F38.wireOp",EDGE,"E58.right")])]}),makeQuery(id+"F39.opExtrude","SWEPT_FACE",FACE,{"disambiguationData":[OSD([sQuery(id+"F38.wireOp",EDGE,"E59.right")])]}),makeQuery(id+"F39.opExtrude","SWEPT_FACE",FACE,{"disambiguationData":[OSD([sQuery(id+"F38.wireOp",EDGE,"E60.right")])]}),makeQuery(id+"F39.opExtrude","SWEPT_FACE",FACE,{"disambiguationData":[OSD([sQuery(id+"F38.wireOp",EDGE,"E61.right")])]})]}),makeQuery(id+"F41.opExtrude","SWEPT_FACE",FACE,{"disambiguationData":[OSD([sQuery(id+"F40.wireOp",EDGE,"E62.left")])]})]}),makeQuery(id+"F43.opExtrude","SWEPT_FACE",FACE,{"disambiguationData":[OSD([sQuery(id+"F42.wireOp",EDGE,"E63.right")])]})]});
            var sketch = newSketch(context, id + "F44", { "sketchPlane" : qUnion([Q0])});
            skLineSegment(sketch, "E64.bottom", {"start": v(-2520.72, 0) * mm, "end": v(-2501.67, 0) * mm});
            skLineSegment(sketch, "E64.top", {"start": v(-2520.72, 19.05) * mm, "end": v(-2501.67, 19.05) * mm});
            skLineSegment(sketch, "E64.left", {"start": v(-2520.72, 0) * mm, "end": v(-2520.72, 19.05) * mm});
            skLineSegment(sketch, "E64.right", {"start": v(-2501.67, 0) * mm, "end": v(-2501.67, 19.05) * mm});
            skSolve(sketch);
        }
        {
            var Q0;
            Q0=makeQuery(id+"F44.imprint","IMPRINT",FACE,{"disambiguationData":[TD([[makeQuery(id+"F44.imprint","IMPRINT",EDGE,{"derivedFrom":sQuery(id+"F44.wireOp",EDGE,"E64.bottom")}),1.0]])]});
            extrude(context, id + "F45", {"entities" : qUnion([Q0]), "operationType" : NewBodyOperationType.ADD, "depth" : 76.2 * mm, "offsetDistance" : 25.4 * mm});
        }
        {
            var Q0;
            Q0=makeQuery(id+"F45.boolean.opBoolean","MERGE",FACE,{"derivedFrom":[makeQuery(id+"F43.opExtrude","CAP_FACE",FACE,{"disambiguationData":[OSD([sQuery(id+"F42.wireOp",EDGE,"E63.bottom"),sQuery(id+"F42.wireOp",EDGE,"E63.top"),sQuery(id+"F42.wireOp",EDGE,"E63.left"),sQuery(id+"F42.wireOp",EDGE,"E63.right")])],"isStart":false}),makeQuery(id+"F45.opExtrude","SWEPT_FACE",FACE,{"disambiguationData":[OSD([sQuery(id+"F44.wireOp",EDGE,"E64.left")])]})]});
            var sketch = newSketch(context, id + "F46", { "sketchPlane" : qUnion([Q0])});
            skLineSegment(sketch, "E65.bottom", {"start": v(-3187.77, 0) * mm, "end": v(-3206.82, 0) * mm});
            skLineSegment(sketch, "E65.top", {"start": v(-3187.77, 19.05) * mm, "end": v(-3206.82, 19.05) * mm});
            skLineSegment(sketch, "E65.left", {"start": v(-3187.77, 0) * mm, "end": v(-3187.77, 19.05) * mm});
            skLineSegment(sketch, "E65.right", {"start": v(-3206.82, 0) * mm, "end": v(-3206.82, 19.05) * mm});
            skSolve(sketch);
        }
        {
            var Q0;
            Q0 = qSketchRegion(id + "F46", true);
            extrude(context, id + "F47", {"entities" : qUnion([Q0]), "operationType" : NewBodyOperationType.ADD, "depth" : 120.88 * mm, "offsetDistance" : 25.4 * mm});
        }
        {
            var Q0;
            Q0=makeQuery(id+"F43.boolean.opBoolean","MERGE",FACE,{"derivedFrom":[makeQuery(id+"F41.boolean.opBoolean","MERGE",FACE,{"derivedFrom":[makeQuery(id+"F39.boolean.opBoolean","MERGE",FACE,{"derivedFrom":[makeQuery(id+"F37.opExtrude","SWEPT_FACE",FACE,{"disambiguationData":[OSD([sQuery(id+"F36.wireOp",EDGE,"E55.left")])]}),makeQuery(id+"F39.opExtrude","SWEPT_FACE",FACE,{"disambiguationData":[OSD([sQuery(id+"F38.wireOp",EDGE,"E56.left")])]}),makeQuery(id+"F39.opExtrude","SWEPT_FACE",FACE,{"disambiguationData":[OSD([sQuery(id+"F38.wireOp",EDGE,"E57.right")])]}),makeQuery(id+"F39.opExtrude","SWEPT_FACE",FACE,{"disambiguationData":[OSD([sQuery(id+"F38.wireOp",EDGE,"E58.right")])]}),makeQuery(id+"F39.opExtrude","SWEPT_FACE",FACE,{"disambiguationData":[OSD([sQuery(id+"F38.wireOp",EDGE,"E59.right")])]}),makeQuery(id+"F39.opExtrude","SWEPT_FACE",FACE,{"disambiguationData":[OSD([sQuery(id+"F38.wireOp",EDGE,"E60.right")])]}),makeQuery(id+"F39.opExtrude","SWEPT_FACE",FACE,{"disambiguationData":[OSD([sQuery(id+"F38.wireOp",EDGE,"E61.right")])]})]}),makeQuery(id+"F41.opExtrude","SWEPT_FACE",FACE,{"disambiguationData":[OSD([sQuery(id+"F40.wireOp",EDGE,"E62.left")])]})]}),makeQuery(id+"F43.opExtrude","SWEPT_FACE",FACE,{"disambiguationData":[OSD([sQuery(id+"F42.wireOp",EDGE,"E63.right")])]})]});
            var sketch = newSketch(context, id + "F48", { "sketchPlane" : qUnion([Q0])});
            skCircle(sketch, "E66", {"center": v(-2239.43, -276.23) * mm, "radius": 4.23 * mm});
            skCircle(sketch, "E67", {"center": v(-2239.43, -549.28) * mm, "radius": 4.23 * mm});
            skCircle(sketch, "E68", {"center": v(-1833.03, -276.23) * mm, "radius": 4.23 * mm});
            skSolve(sketch);
        }
        {
            var Q0;
            Q0 = qSketchRegion(id + "F48", true);
            extrude(context, id + "F49", {"entities" : qUnion([Q0]), "operationType" : NewBodyOperationType.ADD, "depth" : 812.8 * mm, "offsetDistance" : 25.4 * mm});
        }
        {
            var Q0;
            Q0=makeQuery(id+"F2.opExtrude","SWEPT_FACE",FACE,{"disambiguationData":[OSD([sQuery(id+"F0.wireOp",EDGE,"E19.top")])]});
            var sketch = newSketch(context, id + "F50", { "sketchPlane" : qUnion([Q0])});
            skCircle(sketch, "E69", {"center": v(-3486.22, 57.1) * mm, "radius": 9.53 * mm});
            skCircle(sketch, "E70", {"center": v(-3460.82, 57.1) * mm, "radius": 9.53 * mm});
            skCircle(sketch, "E71", {"center": v(-3308.42, 57.1) * mm, "radius": 9.53 * mm});
            skCircle(sketch, "E72", {"center": v(-3283.02, 57.1) * mm, "radius": 9.53 * mm});
            skSolve(sketch);
        }
        {
            var Q0;
            Q0 = qSketchRegion(id + "F50", true);
            extrude(context, id + "F51", {"entities" : qUnion([Q0]), "depth" : 76.2 * mm, "offsetDistance" : 25.4 * mm});
        }
    });
